# Revit family: 728b2ea7d90c4d67a94f402cd976c33f
name_source: partatom
category: Fenêtres
units: mm (PartAtom-declared; Revit-internal decimal feet)

## family parameters
Couper avec des vides une fois chargée = Non
Hôte = Mur
Partagée = Non
Repère de localisation dans la pièce = Non
Toujours verticalement = Oui

## types (2) — shared parameters
Appui = Fenêtre - Appui
Coefficient d'apport thermique solaire = 0.86
Coefficient de transfert thermique (U) = 5.5617 W/(m²·K)
Construction analytique = Grandes fenêtres à vitrage simple
Définir les propriétés thermiques par = Type schématique
Ep. Isolant = 100 mm  [stored 0.328084 ft]
Fenêtre = Fenêtre - Cadre
Fermeture du mur = Extérieur
Hauteur = 2150 mm  [stored 7.05381 ft]
Hauteur de la poignée = 1100 mm  [stored 3.60892 ft]
ID de type de construction = SGL
Opération = SinglePanel
Poignée = Fenêtre - Poignée
Tapées = Fenêtre - Cadre
Transmission de la lumière visible = 0.9
Vitrage = Fenêtre - Vitrage

## per-type parameters (varying)
| type | Largeur |
| 0.80m x 2.15m | 800 mm  [stored 2.62467 ft] |
| 0.90m x 2.15m | 900 mm  [stored 2.95276 ft] |

note: [stored X ft] marks values corroborated as IEEE doubles in the binary element streams (Revit-internal decimal feet)
